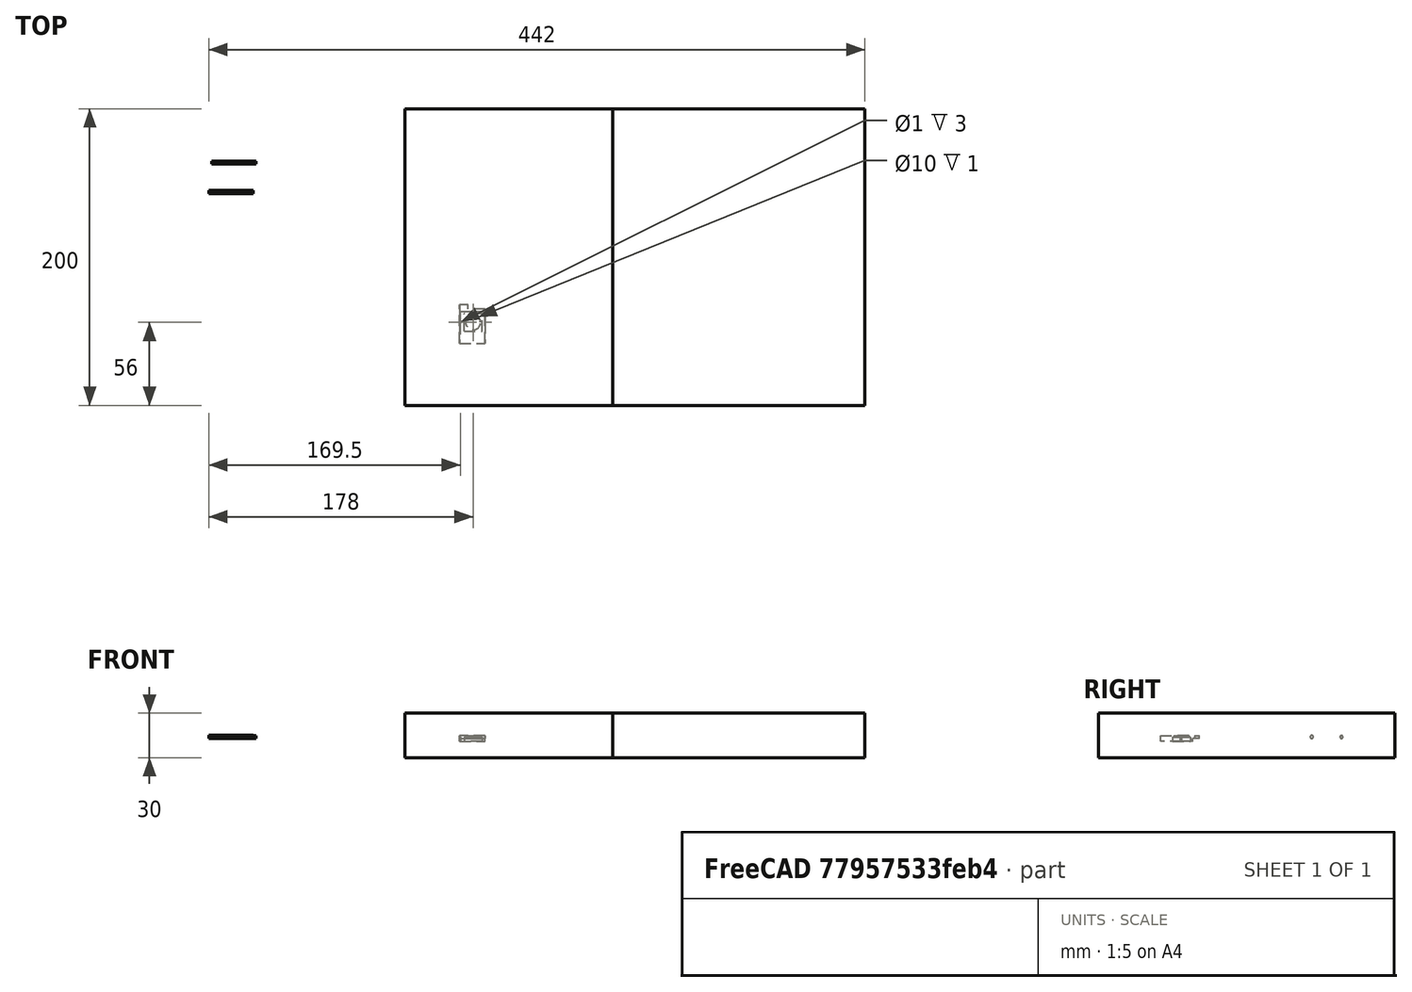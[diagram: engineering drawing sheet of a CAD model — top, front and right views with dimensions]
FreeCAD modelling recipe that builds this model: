
FCSTD DOCUMENT  (FreeCAD 0.17R13522 (Git))
Label: test_panel_para_boton_2
License: CreativeCommons Attribution-ShareAlike
LicenseURL: http://creativecommons.org/licenses/by-sa/4.0/
objects: Part::Cut×39, Part::Feature×33, Part::Box×13, Part::Fuse×8, Part::Part2DObjectPython×7, Part::Cylinder×4, App::DocumentObjectGroup×3, Part::Extrusion×1
note: 105 computed .brp shape members not serialized (recipe doc carries the construction recipe); baked Part::Feature solids carry a one-line shape summary decoded from their .brp

FEATURE [Part::Part2DObjectPython] Line009  # Draft 2D object (typed FeaturePython)
  ChamferSize = 0
  Closed = false
  End = (270.847,20.2,0)
  FilletRadius = 0
  Length = 35.3471
  MakeFace = false
  Points = (2) [(235.5,20.2,0),(270.847,20.2,0)]
  Start = (235.5,20.2,0)
  Subdivisions = 0
FEATURE [Part::Part2DObjectPython] Circle001  # Draft 2D object (typed FeaturePython)
  FirstAngle = 0
  LastAngle = 0
  MakeFace = false
  Placement = pos=(259.67,20.2,0) rot=(0,0,1;0rad)
  Radius = 14
FEATURE [Part::Part2DObjectPython] Line014  # Draft 2D object (typed FeaturePython)
  ChamferSize = 0
  Closed = false
  End = (248.272,28.2144,0)
  FilletRadius = 0
  Length = 13.696
  MakeFace = false
  Placement = pos=(-10,0,-4) rot=(0,0,1;0rad)
  Points = (2) [(269.378,20.2,4),(258.272,28.2144,4)]
  Start = (259.378,20.2,0)
  Subdivisions = 0
FEATURE [Part::Part2DObjectPython] Line015  # Draft 2D object (typed FeaturePython)
  ChamferSize = 0
  Closed = false
  End = (254.876,33.263,0)
  FilletRadius = 0
  Length = 13.7518
  MakeFace = false
  Placement = pos=(-10,0,-4) rot=(0,0,1;0rad)
  Points = (2) [(269.174,20.2,4),(264.876,33.263,4)]
  Start = (259.174,20.2,0)
  Subdivisions = 0
FEATURE [Part::Part2DObjectPython] Line016  # Draft 2D object (typed FeaturePython)
  ChamferSize = 0
  Closed = false
  End = (263.227,33.6931,0)
  FilletRadius = 0
  Length = 14.1488
  MakeFace = false
  Placement = pos=(-10,0,-4) rot=(0,0,1;0rad)
  Points = (2) [(268.97,20.2,4),(273.227,33.6931,4)]
  Start = (258.97,20.2,0)
  Subdivisions = 0
FEATURE [Part::Part2DObjectPython] Line017  # Draft 2D object (typed FeaturePython)
  ChamferSize = 0
  Closed = false
  End = (270.612,28.9289,0)
  FilletRadius = 0
  Length = 14.5511
  MakeFace = false
  Placement = pos=(-10,0,-4) rot=(0,0,1;0rad)
  Points = (2) [(268.97,20.2,4),(280.612,28.9289,4)]
  Start = (258.97,20.2,0)
  Subdivisions = 0
FEATURE [App::DocumentObjectGroup] Construction
  Group = -> [Line009,Circle001,Line014,Line015,Line016,Line017]
FEATURE [Part::Box] Box001  label="Cube"
  AttacherType = Attacher::AttachEngine3D
  Height = 3
  Length = 6
  Placement = pos=(39,81,-108) rot=(0,0,1;0rad)
  Width = 6
FEATURE [Part::Feature] Fusion008001001061001  label="panel_siplays_encoders_dobles_y_spacers"
  Placement = pos=(0,0,-105) rot=(0,0,1;0rad)
  shape: bbox 280 x 210 x 10 mm, 411 faces (baked)
FEATURE [Part::Feature] Fusion003002001  label="el perforador001"
  Placement = pos=(48,115,-108) rot=(0,1,0;3.14159rad)
  shape: bbox 22 x 12 x 18 mm, 19 faces (baked)
FEATURE [Part::Feature] Fusion003002001001  label="el perforador002"
  Placement = pos=(87.5,115,-108) rot=(0,1,0;3.14159rad)
  shape: bbox 22 x 12 x 18 mm, 19 faces (baked)
FEATURE [Part::Cut] Cut001001001002003001008002002004
  Base = -> Fusion008001001061001
  Refine = true
  Tool = -> Fusion003002001
FEATURE [Part::Feature] Fusion003002001001001  label="el perforador003"
  Placement = pos=(127,115,-108) rot=(0,1,0;3.14159rad)
  shape: bbox 22 x 12 x 18 mm, 19 faces (baked)
FEATURE [Part::Cut] Cut001001001002003001008002002005
  Base = -> Cut001001001002003001008002002004
  Refine = true
  Tool = -> Fusion003002001001
FEATURE [Part::Feature] Fusion003002001001001001  label="el perforador004"
  Placement = pos=(166.5,115,-108) rot=(0,1,0;3.14159rad)
  shape: bbox 22 x 12 x 18 mm, 19 faces (baked)
FEATURE [Part::Feature] Fusion003002001001001001001  label="el perforador005"
  Placement = pos=(206,115,-108) rot=(0,1,0;3.14159rad)
  shape: bbox 22 x 12 x 18 mm, 19 faces (baked)
FEATURE [Part::Cut] Cut001001001002003001008002002006
  Base = -> Cut001001001002003001008002002005
  Refine = true
  Tool = -> Fusion003002001001001001
FEATURE [Part::Cut] Cut001001001002003001008002002007
  Base = -> Cut001001001002003001008002002006
  Refine = true
  Tool = -> Fusion003002001001001001001
FEATURE [Part::Feature] Fusion003002001001001001002001001  label="el perforador008"
  Placement = pos=(127,40,-108) rot=(0,1,0;3.14159rad)
  shape: bbox 22 x 12 x 18 mm, 19 faces (baked)
FEATURE [Part::Feature] Fusion003002001001001001002001002  label="el perforador009"
  Placement = pos=(127,80.5,-108) rot=(0,1,0;3.14159rad)
  shape: bbox 22 x 12 x 18 mm, 19 faces (baked)
FEATURE [Part::Feature] Fusion003002001001001001002001  label="el perforador007"
  Placement = pos=(127,55,-108) rot=(0,1,0;3.14159rad)
  shape: bbox 22 x 12 x 18 mm, 19 faces (baked)
FEATURE [Part::Feature] Fusion003002001001001001002  label="el perforador006"
  Placement = pos=(127,95.5,-108) rot=(0,1,0;3.14159rad)
  shape: bbox 22 x 12 x 18 mm, 19 faces (baked)
FEATURE [Part::Cut] Cut001001001002003001008002002008
  Base = -> Cut001001001002003001008002002007
  Refine = true
  Tool = -> Fusion003002001001001
FEATURE [Part::Cut] Cut001001001002003001008002002009
  Base = -> Cut001001001002003001008002002008
  Refine = true
  Tool = -> Fusion003002001001001001002
FEATURE [Part::Cut] Cut001001001002003001008002002010
  Base = -> Cut001001001002003001008002002009
  Refine = true
  Tool = -> Fusion003002001001001001002001
FEATURE [Part::Box] Box001001002002002001003001001004001001001001001001002  label="Cube034"
  AttacherType = Attacher::AttachEngine3D
  Height = 4
  Length = 32
  Placement = pos=(200,15,-108) rot=(0,0,1;0rad)
  Width = 10
FEATURE [Part::Fuse] Fusion003002001001001001002001003
  Base = -> Cut001001001002003001008002002010
  Refine = true
  Tool = -> Box001001002002002001003001001004001001001001001001002
FEATURE [Part::Fuse] Fusion003002001001001001002001004
  Base = -> Box001001002002002001003001001004001001001001001001002
  Refine = true
  Tool = -> Fusion003002001001001001002001003
FEATURE [Part::Fuse] Fusion003002001001001001002001005
  Refine = true
  Tool = -> Fusion003002001001001001002001004
FEATURE [Part::Fuse] Fusion003002001001001001002001006
  Base = -> Box001
  Refine = true
  Tool = -> Fusion003002001001001001002001005
FEATURE [Part::Feature] Fusion003002001001001001002001002001  label="el perforador010"
  Placement = pos=(47,80.5,-108) rot=(0,1,0;3.14159rad)
  shape: bbox 22 x 12 x 18 mm, 19 faces (baked)
FEATURE [Part::Feature] Fusion003002001001001001002001002002  label="el perforador011"
  Placement = pos=(87,80.5,-108) rot=(0,1,0;3.14159rad)
  shape: bbox 22 x 12 x 18 mm, 19 faces (baked)
FEATURE [Part::Feature] Fusion003002001001001001002001001001  label="el perforador012"
  Placement = pos=(87,40,-108) rot=(0,1,0;3.14159rad)
  shape: bbox 22 x 12 x 18 mm, 19 faces (baked)
FEATURE [Part::Feature] Fusion003002001001001001002001001001001  label="el perforador013"
  Placement = pos=(47,40,-108) rot=(0,1,0;3.14159rad)
  shape: bbox 22 x 12 x 18 mm, 19 faces (baked)
FEATURE [Part::Cut] Cut001001001002003001008002002011
  Base = -> Fusion003002001001001001002001006
  Refine = true
  Tool = -> Fusion003002001001001001002001002
FEATURE [Part::Cut] Cut001001001002003001008002002012
  Base = -> Cut001001001002003001008002002011
  Refine = true
  Tool = -> Fusion003002001001001001002001002002
FEATURE [Part::Cut] Cut001001001002003001008002002013
  Base = -> Cut001001001002003001008002002012
  Refine = true
  Tool = -> Fusion003002001001001001002001002001
FEATURE [Part::Cut] Cut001001001002003001008002002014
  Base = -> Cut001001001002003001008002002013
  Refine = true
  Tool = -> Fusion003002001001001001002001001001001
FEATURE [Part::Feature] Fusion003002001001001001002001001001002  label="el perforador014"
  Placement = pos=(220,8,-108) rot=(0.707107,0.707107,0;3.14159rad)
  shape: bbox 12 x 22 x 18 mm, 19 faces (baked)
FEATURE [Part::Cut] Cut001001001002003001008002002015
  Base = -> Cut001001001002003001008002002014
  Refine = true
  Tool = -> Fusion003002001001001001002001001001
FEATURE [Part::Cut] Cut001001001002003001008002002016
  Base = -> Cut001001001002003001008002002015
  Refine = true
  Tool = -> Fusion003002001001001001002001001
FEATURE [Part::Cut] Cut001001001002003001008002002017  label="base solo faltan los leds"
  Base = -> Cut001001001002003001008002002016
  Refine = true
  Tool = -> Fusion003002001001001001002001001001002
FEATURE [Part::Feature] Fusion001001  label="perforador led 3 mm001 rojo com2"
  Placement = pos=(24,43,-108) rot=(0,1,0;3.14159rad)
  shape: bbox 6 x 6 x 10 mm, 13 faces (baked)
FEATURE [Part::Feature] Fusion003002001001001001002001001001003  label="perforador led 3 mm002 rojo nav2"
  Placement = pos=(61,43,-108) rot=(0,1,0;3.14159rad)
  shape: bbox 6 x 6 x 10 mm, 13 faces (baked)
FEATURE [Part::Feature] Fusion003002001001001001002001001001004  label="perforador led 3 mm002 rojo adf2"
  Placement = pos=(101,43,-108) rot=(0,1,0;3.14159rad)
  shape: bbox 6 x 6 x 10 mm, 13 faces (baked)
FEATURE [Part::Feature] Fusion003002001001001001002001001001005  label="perforador led 3 mm001 rojo com1"
  Placement = pos=(24,83.5,-108) rot=(0,1,0;3.14159rad)
  shape: bbox 6 x 6 x 10 mm, 13 faces (baked)
FEATURE [Part::Feature] Fusion003002001001001001002001001001006  label="perforador led 3 mm002 rojo nav1"
  Placement = pos=(61,83.5,-108) rot=(0,1,0;3.14159rad)
  shape: bbox 6 x 6 x 10 mm, 13 faces (baked)
FEATURE [Part::Feature] Fusion003002001001001001002001001001007  label="perforador led 3 mm002 rojo adf1"
  Placement = pos=(101,83.5,-108) rot=(0,1,0;3.14159rad)
  shape: bbox 6 x 6 x 10 mm, 13 faces (baked)
FEATURE [Part::Cut] Cut
  Base = -> Cut001001001002003001008002002017
  Refine = true
  Tool = -> Fusion003002001001001001002001001001005
FEATURE [Part::Cut] Cut001001001002003001008002002018
  Base = -> Cut
  Refine = true
  Tool = -> Fusion003002001001001001002001001001006
FEATURE [Part::Cut] Cut001001001002003001008002002019
  Base = -> Cut001001001002003001008002002018
  Refine = true
  Tool = -> Fusion003002001001001001002001001001007
FEATURE [Part::Cut] Cut001001001002003001008002002020
  Base = -> Cut001001001002003001008002002019
  Refine = true
  Tool = -> Fusion003002001001001001002001001001004
FEATURE [Part::Cut] Cut001001001002003001008002002021
  Base = -> Cut001001001002003001008002002020
  Refine = true
  Tool = -> Fusion003002001001001001002001001001003
FEATURE [Part::Cut] Cut001001001002003001008002002022
  Base = -> Cut001001001002003001008002002021
  Refine = true
  Tool = -> Fusion001001
FEATURE [Part::Feature] Fusion003002001001001001002001001001008  label="perforador led 5 mm sound marker"
  Placement = pos=(40.75,133,-108) rot=(0,1,0;3.14159rad)
  shape: bbox 7.5 x 7.5 x 10 mm, 13 faces (baked)
FEATURE [Part::Feature] Fusion003002001001001001002001001001009  label="perforador led 5 mm sound com1"
  Placement = pos=(80.25,133,-108) rot=(0,1,0;3.14159rad)
  shape: bbox 7.5 x 7.5 x 10 mm, 13 faces (baked)
FEATURE [Part::Feature] Fusion003002001001001001002001001001010  label="perforador led 5 mm sound nav1"
  Placement = pos=(119.75,133,-108) rot=(0,1,0;3.14159rad)
  shape: bbox 7.5 x 7.5 x 10 mm, 13 faces (baked)
FEATURE [Part::Feature] Fusion003002001001001001002001001001011  label="perforador led 5 mm sound dme"
  Placement = pos=(159.25,133,-108) rot=(0,1,0;3.14159rad)
  shape: bbox 7.5 x 7.5 x 10 mm, 13 faces (baked)
FEATURE [Part::Feature] Fusion003002001001001001002001001001012  label="perforador led 5 mm sound adf1"
  Placement = pos=(198.75,133,-108) rot=(0,1,0;3.14159rad)
  shape: bbox 7.5 x 7.5 x 10 mm, 13 faces (baked)
FEATURE [Part::Feature] Fusion003002001001001001002001001001013  label="perforador led 5 mm ON/OFF"
  Placement = pos=(263.5,133,-108) rot=(0,1,0;3.14159rad)
  shape: bbox 7.5 x 7.5 x 10 mm, 13 faces (baked)
FEATURE [Part::Cut] Cut001001001002003001008002002023
  Base = -> Cut001001001002003001008002002022
  Refine = true
  Tool = -> Fusion003002001001001001002001001001013
FEATURE [Part::Cut] Cut001001001002003001008002002024
  Base = -> Cut001001001002003001008002002023
  Refine = true
  Tool = -> Fusion003002001001001001002001001001012
FEATURE [Part::Cut] Cut001001001002003001008002002025
  Base = -> Cut001001001002003001008002002024
  Refine = true
  Tool = -> Fusion003002001001001001002001001001011
FEATURE [Part::Cut] Cut001001001002003001008002002026
  Base = -> Cut001001001002003001008002002025
  Refine = true
  Tool = -> Fusion003002001001001001002001001001010
FEATURE [Part::Cut] Cut001001001002003001008002002027
  Base = -> Cut001001001002003001008002002026
  Refine = true
  Tool = -> Fusion003002001001001001002001001001009
FEATURE [Part::Cut] Cut001001001002003001008002002028
  Base = -> Cut001001001002003001008002002027
  Refine = true
  Tool = -> Fusion003002001001001001002001001001008
FEATURE [Part::Box] Box  label="Cube035"
  AttacherType = Attacher::AttachEngine3D
  Height = 10
  Length = 300
  Placement = pos=(-8,153.85,-111) rot=(0,0,1;0rad)
  Width = 120
FEATURE [Part::Cut] Cut001001001002003001008002002029  label="panel sin letras"
  Base = -> Cut001001001002003001008002002028
  Refine = true
  Tool = -> Box
FEATURE [Part::Box] Box001001002002002001003001001004001001001001001001003  label="cortador saca parte izquierda"
  AttacherType = Attacher::AttachEngine3D
  Height = 30
  Length = 140
  Placement = pos=(-10,-10,-119) rot=(0,0,1;0rad)
  Width = 200
FEATURE [Part::Box] Box001001002002002001003001001004001001001001001001004  label="cortador saca parte derecha"
  AttacherType = Attacher::AttachEngine3D
  Height = 30
  Length = 170
  Placement = pos=(130,-10,-119) rot=(0,0,1;0rad)
  Width = 200
FEATURE [Part::Cylinder] Cylinder  label="clavija agujereadora1_1"
  Angle = 360
  AttacherType = Attacher::AttachEngine3D
  Height = 30
  Placement = pos=(115,111.85,-106) rot=(0,1,0;1.5708rad)
  Radius = 1.05
FEATURE [Part::Cylinder] Cylinder001  label="clavija agujereadora2_1"
  Angle = 360
  AttacherType = Attacher::AttachEngine3D
  Height = 30
  Placement = pos=(115,37.85,-106) rot=(0,1,0;1.5708rad)
  Radius = 1.05
FEATURE [Part::Cylinder] Cylinder002  label="clavija empalmadora1"
  Angle = 360
  AttacherType = Attacher::AttachEngine3D
  Height = 29.8
  Placement = pos=(-140,153.85,-105) rot=(0,1,0;1.5708rad)
  Radius = 1
FEATURE [Part::Cut] Cut001001001002003001008002002030
  Base = -> Cut001001001002003001008002002029
  Refine = true
  Tool = -> Cylinder
FEATURE [Part::Cut] Cut001001001002003001008002002031  label="panel sin letras con agujeros clavijas"
  Base = -> Cut001001001002003001008002002030
  Refine = true
  Tool = -> Cylinder001
FEATURE [App::DocumentObjectGroup] Group  label="cortadores principales"
  Group = -> [Box001001002002002001003001001004001001001001001001003,Box001001002002002001003001001004001001001001001001004]
FEATURE [Part::Cylinder] Cylinder003  label="clavija hace agujero"
  Angle = 360
  AttacherType = Attacher::AttachEngine3D
  Height = 30
  Placement = pos=(-142,133.85,-105) rot=(0,1,0;1.5708rad)
  Radius = 1.05
FEATURE [App::DocumentObjectGroup] Group001  label="clavijas"
  Group = -> [Cylinder003,Cylinder002]
FEATURE [Part::Box] Box001001002002002001003001001004001001001001001001006  label="fleje abajo"
  AttacherType = Attacher::AttachEngine3D
  Height = 4
  Length = 280
  Placement = pos=(0,-4,-108) rot=(0,0,1;0rad)
  Width = 4
FEATURE [Part::Fuse] Fusion
  Base = -> Cut001001001002003001008002002031
  Refine = true
  Tool = -> Box001001002002002001003001001004001001001001001001006
FEATURE [Part::Feature] Cylinder002001  label="clavija empalmadora une frente base"
  Placement = pos=(30,-2,-134) rot=(0,0,1;1.5708rad)
  shape: bbox 2 x 2 x 29.8 mm, 3 faces (baked)
FEATURE [Part::Feature] Cylinder002001001  label="clavija empalmadora une frente base2"
  Placement = pos=(250,-2,-134) rot=(0,0,1;1.5708rad)
  shape: bbox 2 x 2 x 29.8 mm, 3 faces (baked)
FEATURE [Part::Fuse] Fusion003002001001001001002001001001014
  Base = -> Fusion
  Refine = true
  Tool = -> Cylinder002001
FEATURE [Part::Fuse] Fusion003002001001001001002001001001015  label="frente con clavijas sin letras"
  Base = -> Cylinder002001001
  Refine = true
  Tool = -> Fusion003002001001001001002001001001014
FEATURE [Part::Box] Box001001002002002001003001001004001001001001001001007  label="cortador clavijas"
  AttacherType = Attacher::AttachEngine3D
  Height = 4
  Length = 280
  Placement = pos=(0,0,-153) rot=(1,0,0;1.5708rad)
  Width = 30
FEATURE [Part::Cut] Cut001001001002003001008002002032  label="frente con clavijas de 15 sin letras"
  Base = -> Fusion003002001001001001002001001001015
  Refine = true
  Tool = -> Box001001002002002001003001001004001001001001001001007
FEATURE [Part::Box] Box001001002002002001003001001004001001001001001001008  label="Cube036"
  AttacherType = Attacher::AttachEngine3D
  Height = 1
  Length = 14
  Width = 14
FEATURE [Part::Part2DObjectPython] Circle002  # Draft 2D object (typed FeaturePython)
  FirstAngle = 0
  LastAngle = 0
  MakeFace = true
  Placement = pos=(7,7,1) rot=(0,0,1;3.14159rad)
  Radius = 5
FEATURE [Part::Extrusion] Extrude
  Base = -> Circle002
  Dir = (0,0,1)
  DirMode = 2
  FaceMakerClass = Part::FaceMakerBullseye
  LengthFwd = 10
  LengthRev = 0
  Placement = pos=(0,0,-6) rot=(0,0,1;0rad)
  Solid = false
  Symmetric = false
FEATURE [Part::Cut] Cut001001001002003001008002002033  label="circulo_para_botones"
  Base = -> Box001001002002002001003001001004001001001001001001008
  Placement = pos=(-28,0,0) rot=(0,0,1;0rad)
  Refine = true
  Tool = -> Extrude
FEATURE [Part::Feature] Cut001001001002003001008002002033001  label="circulo_para_botones001"
  Placement = pos=(29,39,-105) rot=(0,0,1;0rad)
  shape: bbox 14 x 14 x 1 mm, 7 faces (baked)
FEATURE [Part::Fuse] Fusion003002001001001001002001001001016
  Base = -> Cut001001001002003001008002002032
  Refine = true
  Tool = -> Cut001001001002003001008002002033001
FEATURE [Part::Box] Box001001002002002001003001001004001001001001001001009  label="Cube037"
  AttacherType = Attacher::AttachEngine3D
  Height = 60
  Length = 300
  Placement = pos=(44,-31,-120) rot=(0,0,1;0rad)
  Width = 250
FEATURE [Part::Cut] Cut001001001002003001008002002033002
  Base = -> Fusion003002001001001001002001001001016
  Refine = true
  Tool = -> Box001001002002002001003001001004001001001001001001009
FEATURE [Part::Box] Box001001002002002001003001001004001001001001001001010  label="Cube038"
  AttacherType = Attacher::AttachEngine3D
  Height = 10
  Length = 50
  Placement = pos=(-23,-26,-113) rot=(0,0,1;0rad)
  Width = 300
FEATURE [Part::Box] Box001001002002002001003001001004001001001001001001011  label="Cube039"
  AttacherType = Attacher::AttachEngine3D
  Height = 10
  Length = 58
  Placement = pos=(8,58,-107) rot=(0,0,1;0rad)
  Width = 150
FEATURE [Part::Cut] Cut001001001002003001008002002033003
  Base = -> Cut001001001002003001008002002033002
  Refine = true
  Tool = -> Box001001002002002001003001001004001001001001001001010
FEATURE [Part::Cut] Cut001001001002003001008002002033004
  Base = -> Cut001001001002003001008002002033003
  Refine = true
  Tool = -> Box001001002002002001003001001004001001001001001001011
FEATURE [Part::Box] Box001001002002002001003001001004001001001001001001012  label="Cube040"
  AttacherType = Attacher::AttachEngine3D
  Height = 200
  Length = 60
  Placement = pos=(-36,-18,-136) rot=(0,0,1;0rad)
  Width = 250
FEATURE [Part::Feature] Box001001002002002001003001001004001001001001001001012001  label="Cube041"
  Placement = pos=(200,-27,-136) rot=(0,0,1;0rad)
  shape: bbox 60 x 250 x 60 mm, 6 faces (baked)
FEATURE [Part::Feature] Box001001002002002001003001001004001001001001001001012002  label="Cube042"
  Placement = pos=(-2,-218,-136) rot=(0,0,1;0rad)
  shape: bbox 60 x 250 x 60 mm, 6 faces (baked)
FEATURE [Part::Feature] Box001001002002002001003001001004001001001001001001012003  label="Cube043"
  Placement = pos=(-5,60,-136) rot=(0,0,1;0rad)
  shape: bbox 60 x 250 x 60 mm, 6 faces (baked)
FEATURE [Part::Cut] Cut001001001002003001008002002033005
  Base = -> Cut001001001002003001008002002033
  Refine = true
  Tool = -> Box001001002002002001003001001004001001001001001001012
FEATURE [Part::Cut] Cut001001001002003001008002002033006
  Base = -> Cut001001001002003001008002002033004
  Refine = true
  Tool = -> Box001001002002002001003001001004001001001001001001012003
FEATURE [Part::Cut] Cut001001001002003001008002002033007
  Base = -> Cut001001001002003001008002002033006
  Refine = true
  Tool = -> Box001001002002002001003001001004001001001001001001012001
FEATURE [Part::Cut] Cut001001001002003001008002002033008
  Base = -> Cut001001001002003001008002002033007
  Refine = true
  Tool = -> Box001001002002002001003001001004001001001001001001012002
FEATURE [Part::Box] Box001001002002002001003001001004001001001001001001012004  label="Cube044"
  AttacherType = Attacher::AttachEngine3D
  Height = 60
  Length = 60
  Placement = pos=(-36,12,-150) rot=(0,0,1;0rad)
  Width = 60
FEATURE [Part::Cut] Cut001001001002003001008002002033009
  Base = -> Cut001001001002003001008002002033008
  Refine = true
  Tool = -> Box001001002002002001003001001004001001001001001001012004
